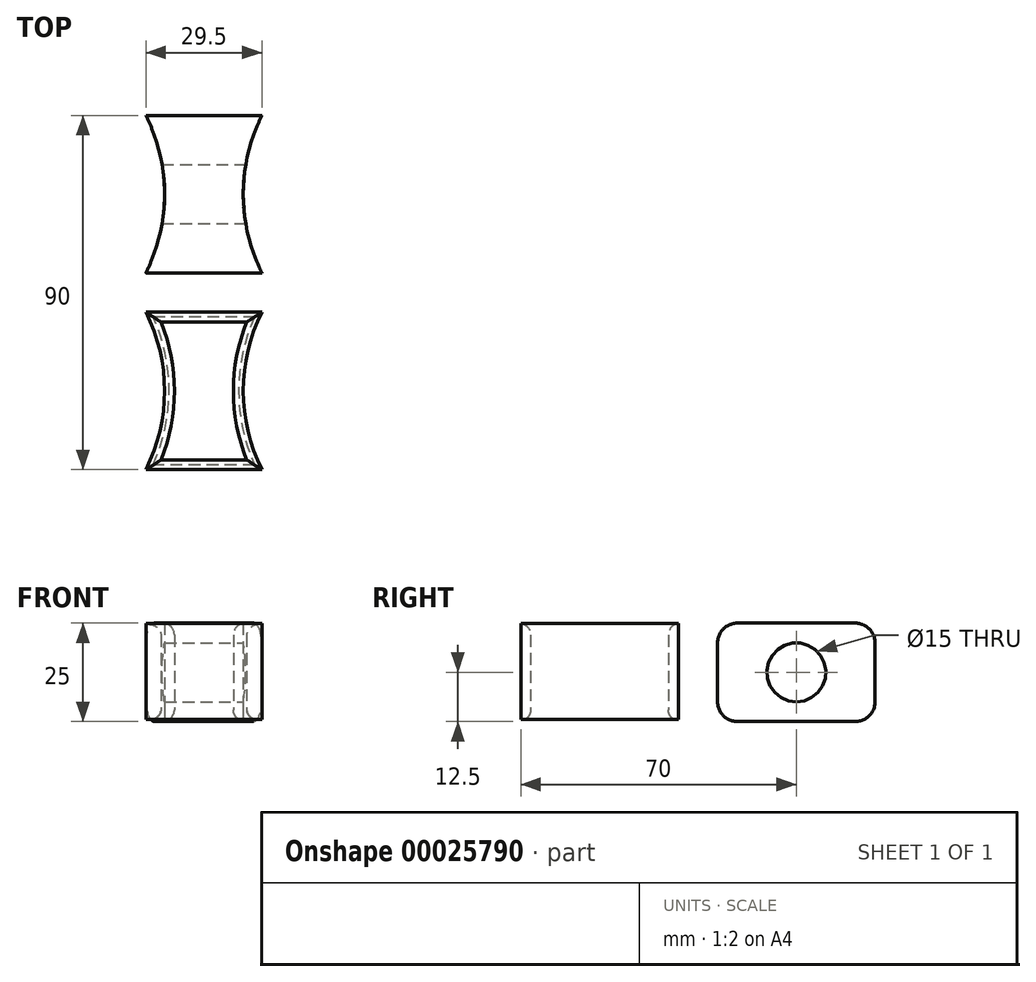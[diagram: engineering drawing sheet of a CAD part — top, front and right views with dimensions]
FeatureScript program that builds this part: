
annotation { "Feature Type Name" : "Feature", "Feature Type Description" : "" }
export const myFeature = defineFeature(function(context is Context, id is Id, definition is map)
    precondition{}
    {
        {
            var Q0;
            Q0=qCreatedBy(makeId("Top.planeOp"),FACE);
            var sketch = newSketch(context, id + "F0", { "sketchPlane" : qUnion([Q0])});
            skLineSegment(sketch, "E0", {"start": v(0, 0) * mm, "end": v(0, -20) * mm, "construction": true});
            skLineSegment(sketch, "E1", {"start": v(0, 0) * mm, "end": v(-10, 0) * mm, "construction": true});
            skLineSegment(sketch, "E2", {"start": v(0, -20) * mm, "end": v(-14.75, -20) * mm});
            skLineSegment(sketch, "E3.MirrorCS", {"start": v(0, 20) * mm, "end": v(-14.75, 20) * mm});
            skArc(sketch, "E4", {"start": v(-14.75, -20) * mm, "mid": v(-10, 0) * mm, "end": v(-14.75, 20) * mm});
            skLineSegment(sketch, "E5.MirrorCS", {"start": v(0, -20) * mm, "end": v(14.75, -20) * mm});
            skArc(sketch, "E6.MirrorCS", {"start": v(14.75, -20) * mm, "mid": v(10, 0) * mm, "end": v(14.75, 20) * mm});
            skLineSegment(sketch, "E7.MirrorCS", {"start": v(0, 20) * mm, "end": v(14.75, 20) * mm});
            skSolve(sketch);
        }
        {
            var Q0;
            Q0=makeQuery(id+"F0.imprint","IMPRINT",FACE,{"disambiguationData":[TD([[makeQuery(id+"F0.imprint","IMPRINT",EDGE,{"derivedFrom":sQuery(id+"F0.wireOp",EDGE,"E2")}),-1.0]])]});
            extrude(context, id + "F1", {"entities" : qUnion([Q0]), "depth" : 25 * mm});
        }
        {
            var Q0;
            Q0=makeQuery(id+"F1.opExtrude","SWEPT_BODY",BODY,{"disambiguationData":[OSD([sQuery(id+"F0.wireOp",EDGE,"E2"),sQuery(id+"F0.wireOp",EDGE,"E3.MirrorCS"),sQuery(id+"F0.wireOp",EDGE,"E4"),sQuery(id+"F0.wireOp",EDGE,"E5.MirrorCS"),sQuery(id+"F0.wireOp",EDGE,"E6.MirrorCS"),sQuery(id+"F0.wireOp",EDGE,"E7.MirrorCS")])]});
            var Q1;
            Q1=makeQuery(id+"F1.opExtrude","SWEPT_FACE",FACE,{"disambiguationData":[OSD([sQuery(id+"F0.wireOp",EDGE,"E2"),sQuery(id+"F0.wireOp",EDGE,"E5.MirrorCS")])]});
            transform(context, id + "F2", {"entities" : qUnion([Q0]), "transformType" : TransformType.TRANSLATION_DISTANCE, "transformDirection" : qUnion([Q1]), "distance" : 50 * mm, "makeCopy" : true});
        }
        {
            var Q0;
            Q0=qCreatedBy(makeId("Right.planeOp"),FACE);
            var sketch = newSketch(context, id + "F3", { "sketchPlane" : qUnion([Q0])});
            skLineSegment(sketch, "E8", {"start": v(0, 0) * mm, "end": v(0, 25) * mm, "construction": true});
            skCircle(sketch, "E9", {"center": v(0, 12.5) * mm, "radius": 7.5 * mm});
            skSolve(sketch);
        }
        {
            var Q0;
            Q0 = qSketchRegion(id + "F3", true);
            extrude(context, id + "F4", {"entities" : qUnion([Q0]), "operationType" : NewBodyOperationType.REMOVE, "endBound" : BoundingType.SYMMETRIC, "oppositeDirection" : true, "depth" : 25 * mm});
        }
        {
            var Q0;
            Q0=makeQuery(id+"F2.opPattern","COPY",FACE,{"derivedFrom":makeQuery(id+"F1.opExtrude","CAP_FACE",FACE,{"disambiguationData":[OSD([sQuery(id+"F0.wireOp",EDGE,"E2"),sQuery(id+"F0.wireOp",EDGE,"E3.MirrorCS"),sQuery(id+"F0.wireOp",EDGE,"E4"),sQuery(id+"F0.wireOp",EDGE,"E5.MirrorCS"),sQuery(id+"F0.wireOp",EDGE,"E6.MirrorCS"),sQuery(id+"F0.wireOp",EDGE,"E7.MirrorCS")])],"isStart":true}),"instanceName":"1"});
            var Q1;
            Q1=makeQuery(id+"F2.opPattern","COPY",FACE,{"derivedFrom":makeQuery(id+"F1.opExtrude","CAP_FACE",FACE,{"disambiguationData":[OSD([sQuery(id+"F0.wireOp",EDGE,"E2"),sQuery(id+"F0.wireOp",EDGE,"E3.MirrorCS"),sQuery(id+"F0.wireOp",EDGE,"E4"),sQuery(id+"F0.wireOp",EDGE,"E5.MirrorCS"),sQuery(id+"F0.wireOp",EDGE,"E6.MirrorCS"),sQuery(id+"F0.wireOp",EDGE,"E7.MirrorCS")])],"isStart":false}),"instanceName":"1"});
            shell(context, id + "F5", {"entities" : qUnion([Q0, Q1]), "thickness" : 2.5 * mm});
        }
        {
            var Q0;
            {var subQ0=sQuery(id+"F0.wireOp",EDGE,"E6.MirrorCS");Q0=makeQuery(id+"F5.opShell","OFFSET_EDGE",EDGE,{"disambiguationData":[OSD([subQ0]),TDD([makeQuery(id+"F2.opPattern","COPY",EDGE,{"derivedFrom":makeQuery(id+"F1.opExtrude","CAP_EDGE",EDGE,{"disambiguationData":[OSD([subQ0])],"isStart":false}),"instanceName":"1"})])]});}
            var Q1;
            {var subQ0=sQuery(id+"F0.wireOp",EDGE,"E2");var subQ1=sQuery(id+"F0.wireOp",EDGE,"E5.MirrorCS");Q1=makeQuery(id+"F5.opShell","OFFSET_EDGE",EDGE,{"disambiguationData":[OSD([subQ0,subQ1]),TDD([makeQuery(id+"F2.opPattern","COPY",EDGE,{"derivedFrom":makeQuery(id+"F1.opExtrude","CAP_EDGE",EDGE,{"disambiguationData":[OSD([subQ0,subQ1])],"isStart":false}),"instanceName":"1"})])]});}
            var Q2;
            {var subQ0=sQuery(id+"F0.wireOp",EDGE,"E4");Q2=makeQuery(id+"F5.opShell","OFFSET_EDGE",EDGE,{"disambiguationData":[OSD([subQ0]),TDD([makeQuery(id+"F2.opPattern","COPY",EDGE,{"derivedFrom":makeQuery(id+"F1.opExtrude","CAP_EDGE",EDGE,{"disambiguationData":[OSD([subQ0])],"isStart":false}),"instanceName":"1"})])]});}
            var Q3;
            {var subQ0=sQuery(id+"F0.wireOp",EDGE,"E3.MirrorCS");var subQ1=sQuery(id+"F0.wireOp",EDGE,"E7.MirrorCS");Q3=makeQuery(id+"F5.opShell","OFFSET_EDGE",EDGE,{"disambiguationData":[OSD([subQ0,subQ1]),TDD([makeQuery(id+"F2.opPattern","COPY",EDGE,{"derivedFrom":makeQuery(id+"F1.opExtrude","CAP_EDGE",EDGE,{"disambiguationData":[OSD([subQ0,subQ1])],"isStart":false}),"instanceName":"1"})])]});}
            var Q4;
            {var subQ0=sQuery(id+"F0.wireOp",EDGE,"E6.MirrorCS");Q4=makeQuery(id+"F5.opShell","OFFSET_EDGE",EDGE,{"disambiguationData":[OSD([subQ0]),TDD([makeQuery(id+"F2.opPattern","COPY",EDGE,{"derivedFrom":makeQuery(id+"F1.opExtrude","CAP_EDGE",EDGE,{"disambiguationData":[OSD([subQ0])],"isStart":true}),"instanceName":"1"})])]});}
            var Q5;
            {var subQ0=sQuery(id+"F0.wireOp",EDGE,"E4");Q5=makeQuery(id+"F5.opShell","OFFSET_EDGE",EDGE,{"disambiguationData":[OSD([subQ0]),TDD([makeQuery(id+"F2.opPattern","COPY",EDGE,{"derivedFrom":makeQuery(id+"F1.opExtrude","CAP_EDGE",EDGE,{"disambiguationData":[OSD([subQ0])],"isStart":true}),"instanceName":"1"})])]});}
            var Q6;
            {var subQ0=sQuery(id+"F0.wireOp",EDGE,"E3.MirrorCS");var subQ1=sQuery(id+"F0.wireOp",EDGE,"E7.MirrorCS");Q6=makeQuery(id+"F5.opShell","OFFSET_EDGE",EDGE,{"disambiguationData":[OSD([subQ0,subQ1]),TDD([makeQuery(id+"F2.opPattern","COPY",EDGE,{"derivedFrom":makeQuery(id+"F1.opExtrude","CAP_EDGE",EDGE,{"disambiguationData":[OSD([subQ0,subQ1])],"isStart":true}),"instanceName":"1"})])]});}
            var Q7;
            {var subQ0=sQuery(id+"F0.wireOp",EDGE,"E2");var subQ1=sQuery(id+"F0.wireOp",EDGE,"E5.MirrorCS");Q7=makeQuery(id+"F5.opShell","OFFSET_EDGE",EDGE,{"disambiguationData":[OSD([subQ0,subQ1]),TDD([makeQuery(id+"F2.opPattern","COPY",EDGE,{"derivedFrom":makeQuery(id+"F1.opExtrude","CAP_EDGE",EDGE,{"disambiguationData":[OSD([subQ0,subQ1])],"isStart":true}),"instanceName":"1"})])]});}
            fillet(context, id + "F6", {"entities" : qUnion([Q0, Q1, Q2, Q3, Q4, Q5, Q6, Q7]), "radius" : 3 * mm, "tangentPropagation" : true, "allowEdgeOverflow" : false});
        }
        {
            var Q0;
            Q0=qCreatedBy(makeId("Top.planeOp"),FACE);
            var sketch = newSketch(context, id + "F7", { "sketchPlane" : qUnion([Q0])});
            skLineSegment(sketch, "E10.bottom", {"start": v(-18.18, -26.2) * mm, "end": v(17.4, -26.2) * mm});
            skLineSegment(sketch, "E10.top", {"start": v(-18.18, -71.93) * mm, "end": v(17.4, -71.93) * mm});
            skLineSegment(sketch, "E10.left", {"start": v(-18.18, -26.2) * mm, "end": v(-18.18, -71.93) * mm});
            skLineSegment(sketch, "E10.right", {"start": v(17.4, -26.2) * mm, "end": v(17.4, -71.93) * mm});
            skSolve(sketch);
        }
        {
            var Q0;
            Q0 = qSketchRegion(id + "F7", true);
            extrude(context, id + "F8", {"entities" : qUnion([Q0]), "depth" : .5 * mm});
        }
        {
            var Q0;
            Q0=makeQuery(id+"F8.opExtrude","SWEPT_BODY",BODY,{"disambiguationData":[OSD([sQuery(id+"F7.wireOp",EDGE,"E10.bottom"),sQuery(id+"F7.wireOp",EDGE,"E10.top"),sQuery(id+"F7.wireOp",EDGE,"E10.left"),sQuery(id+"F7.wireOp",EDGE,"E10.right")])]});
            var Q1;
            Q1=makeQuery(id+"F2.opPattern","COPY",BODY,{"derivedFrom":makeQuery(id+"F1.opExtrude","SWEPT_BODY",BODY,{"disambiguationData":[OSD([sQuery(id+"F0.wireOp",EDGE,"E2"),sQuery(id+"F0.wireOp",EDGE,"E3.MirrorCS"),sQuery(id+"F0.wireOp",EDGE,"E4"),sQuery(id+"F0.wireOp",EDGE,"E5.MirrorCS"),sQuery(id+"F0.wireOp",EDGE,"E6.MirrorCS"),sQuery(id+"F0.wireOp",EDGE,"E7.MirrorCS")])]}),"instanceName":"1"});
            booleanBodies(context, id + "F9", {"operationType" : BooleanOperationType.SUBTRACTION, "tools" : qUnion([Q0]), "targets" : qUnion([Q1])});
        }
        {
            var Q0;
            Q0=makeQuery(id+"F1.opExtrude","CAP_EDGE",EDGE,{"disambiguationData":[OSD([sQuery(id+"F0.wireOp",EDGE,"E2"),sQuery(id+"F0.wireOp",EDGE,"E5.MirrorCS")])],"isStart":false});
            var Q1;
            Q1=makeQuery(id+"F1.opExtrude","CAP_EDGE",EDGE,{"disambiguationData":[OSD([sQuery(id+"F0.wireOp",EDGE,"E2"),sQuery(id+"F0.wireOp",EDGE,"E5.MirrorCS")])],"isStart":true});
            var Q2;
            Q2=makeQuery(id+"F1.opExtrude","CAP_EDGE",EDGE,{"disambiguationData":[OSD([sQuery(id+"F0.wireOp",EDGE,"E3.MirrorCS"),sQuery(id+"F0.wireOp",EDGE,"E7.MirrorCS")])],"isStart":true});
            var Q3;
            Q3=makeQuery(id+"F1.opExtrude","CAP_EDGE",EDGE,{"disambiguationData":[OSD([sQuery(id+"F0.wireOp",EDGE,"E3.MirrorCS"),sQuery(id+"F0.wireOp",EDGE,"E7.MirrorCS")])],"isStart":false});
            fillet(context, id + "F10", {"entities" : qUnion([Q0, Q1, Q2, Q3]), "radius" : 5 * mm, "tangentPropagation" : true, "allowEdgeOverflow" : false});
        }
    });
